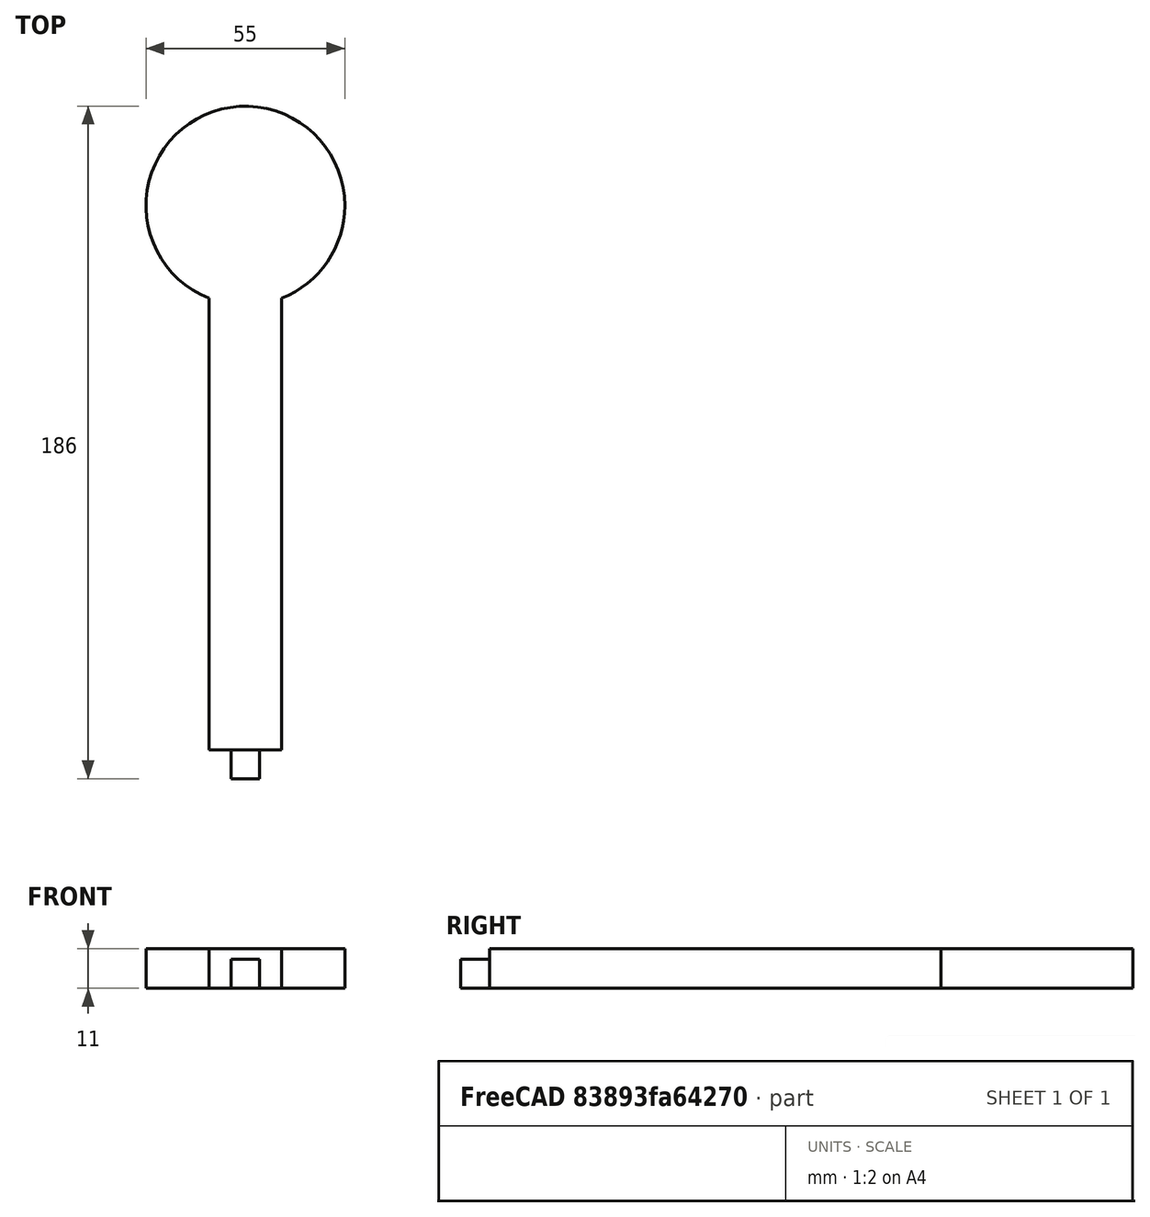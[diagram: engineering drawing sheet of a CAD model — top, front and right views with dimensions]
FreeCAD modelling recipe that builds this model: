
FCSTD DOCUMENT  (FreeCAD 0.19R)
Label: 26erTop
License: All rights reserved
LicenseURL: http://en.wikipedia.org/wiki/All_rights_reserved
objects: Sketcher::SketchObject×3, PartDesign::Pad×3, PartDesign::Body×1, Mesh::Feature×1
note: 10 computed .brp shape members not serialized (recipe doc carries the construction recipe); baked Part::Feature solids carry a one-line shape summary decoded from their .brp

FEATURE [Sketcher::SketchObject] Sketch
  FullyConstrained = true
  MapMode = 5
  Support = -> [XY_Plane]
  sketch-geometry (4):
    g0: LineSegment StartX=10 StartY=150 StartZ=0 EndX=10 EndY=278 EndZ=0
    g1: LineSegment StartX=10 StartY=278 StartZ=0 EndX=-10 EndY=278 EndZ=0
    g2: LineSegment StartX=-10 StartY=278 StartZ=0 EndX=-10 EndY=150 EndZ=0
    g3: LineSegment StartX=-10 StartY=150 StartZ=0 EndX=10 EndY=150 EndZ=0
  constraints (10):
    c: Vertical(g0)
    c: Coincident(g0,g1)
    c: Coincident(g1,g2)
    c: Symmetric(g0,g1,g-2)
    c: Symmetric(g0,g2,g-2)
    c: Distance(g1) = 20
    c: DistanceY(g0) = 278
    c: Coincident(g3,g2)
    c: Coincident(g3,g0)
    c: DistanceY(g0) = 150
FEATURE [PartDesign::Pad] Pad
  Direction = (1,1,1)
  Length = 11
  Length2 = 100
  Profile = -> Sketch
  Type = 0
FEATURE [Sketcher::SketchObject] Sketch001
  FullyConstrained = true
  MapMode = 5
  Placement = pos=(0,0,11) rot=(0,0,1;0rad)
  Support = -> [Pad]
  sketch-geometry (2):
    g0: Circle CenterX=0 CenterY=300.5 CenterZ=0 NormalX=0 NormalY=0 NormalZ=1 AngleXU=0 Radius=27.5
    g1: LineSegment StartX=-25 StartY=328 StartZ=0 EndX=25 EndY=328 EndZ=0
  constraints (6):
    c: PointOnObject(g0,g-2)
    c: Radius(g0) = 27.5
    c: Symmetric(g1,g1,g-2)
    c: Distance(g1) = 50
    c: DistanceY(g1) = 328
    c: Tangent(g0,g1)
FEATURE [PartDesign::Pad] Pad001
  BaseFeature = -> Pad
  Direction = (1,1,1)
  Length = 11
  Length2 = 100
  Profile = -> Sketch001
  Reversed = true
  Type = 0
FEATURE [Sketcher::SketchObject] Sketch002
  FullyConstrained = true
  MapMode = 5
  Placement = pos=(0,150,0) rot=(1,0,0;1.5708rad)
  Support = -> [Pad001]
  sketch-geometry (4):
    g0: LineSegment StartX=-3.95 StartY=8 StartZ=0 EndX=3.95 EndY=8 EndZ=0
    g1: LineSegment StartX=3.95 StartY=8 StartZ=0 EndX=3.95 EndY=0 EndZ=0
    g2: LineSegment StartX=3.95 StartY=0 StartZ=0 EndX=-3.95 EndY=0 EndZ=0
    g3: LineSegment StartX=-3.95 StartY=0 StartZ=0 EndX=-3.95 EndY=8 EndZ=0
  constraints (11):
    c: Coincident(g0,g1)
    c: Coincident(g1,g2)
    c: Coincident(g2,g3)
    c: Coincident(g3,g0)
    c: Horizontal(g0)
    c: Horizontal(g2)
    c: Vertical(g1)
    c: Vertical(g3)
    c: Distance(g0) = 7.9
    c: Distance(g1) = 8
    c: Symmetric(g1,g2,g-1)
FEATURE [PartDesign::Pad] Pad002
  BaseFeature = -> Pad001
  Direction = (1,1,1)
  Length = 8
  Length2 = 100
  Profile = -> Sketch002
  Type = 0
FEATURE [PartDesign::Body] Body
  Group = -> [Sketch,Pad,Sketch001,Pad001,Sketch002,Pad002]
  Origin = -> Origin
  Tip = -> Pad002
FEATURE [Mesh::Feature] Mesh  label="Pad002 (Meshed)"
